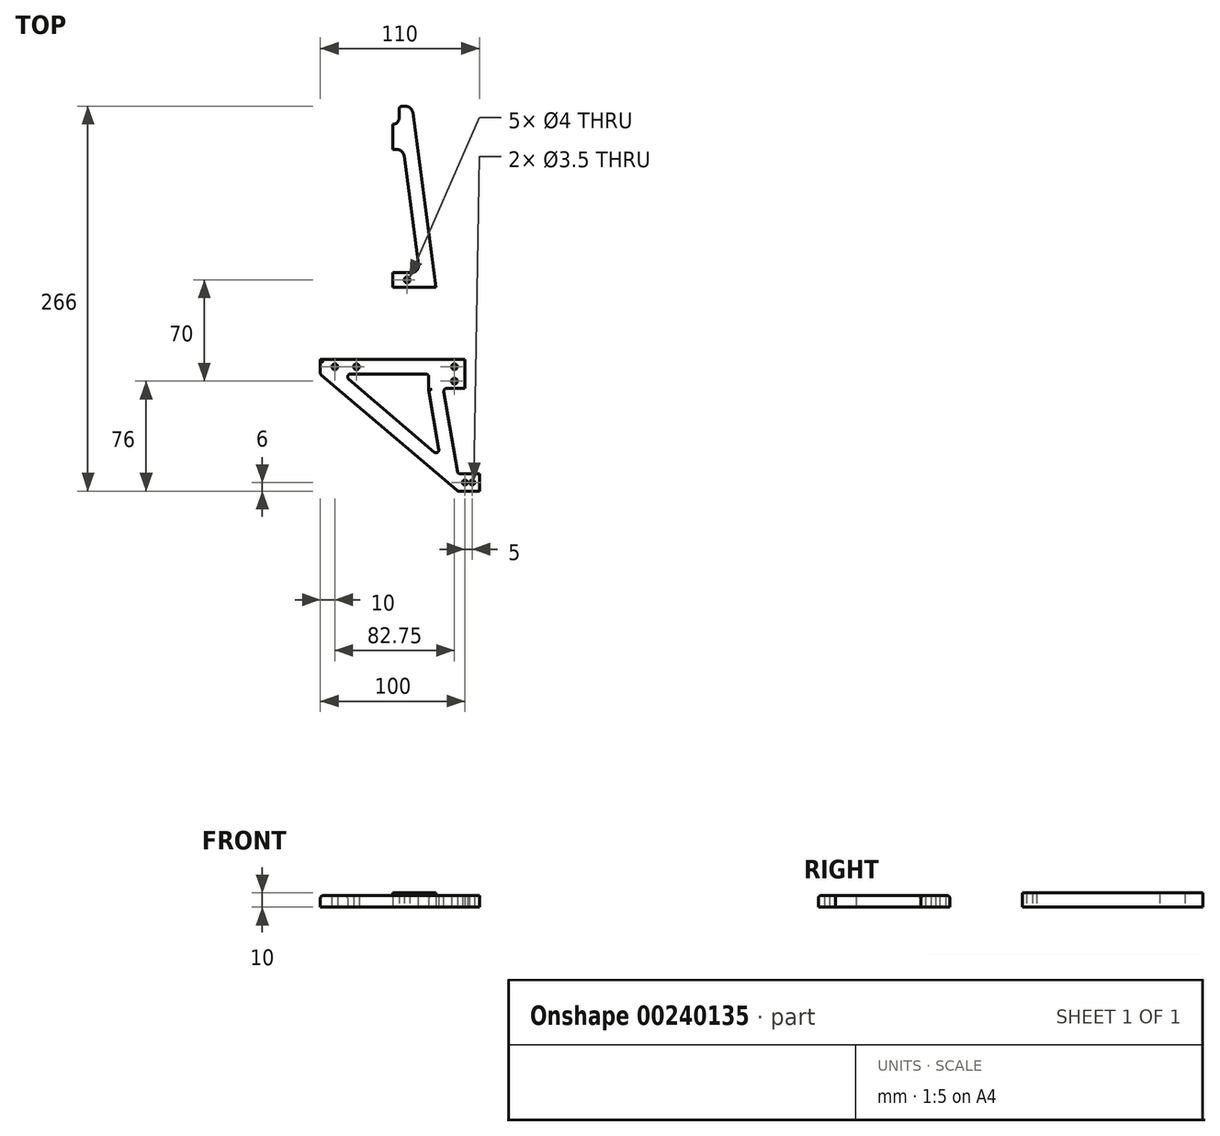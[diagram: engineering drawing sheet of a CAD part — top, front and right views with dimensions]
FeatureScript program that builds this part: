
annotation { "Feature Type Name" : "Feature", "Feature Type Description" : "" }
export const myFeature = defineFeature(function(context is Context, id is Id, definition is map)
    precondition{}
    {
        {
            var Q0;
            Q0=qCreatedBy(makeId("Top.planeOp"),FACE);
            var sketch = newSketch(context, id + "F0", { "sketchPlane" : qUnion([Q0])});
            skLineSegment(sketch, "E0.top", {"start": v(0, 75) * mm, "end": v(-30, 75) * mm});
            skPoint(sketch, "E0.middle", {"position": v(0, 0) * mm});
            skLineSegment(sketch, "E1", {"start": v(-30, 75) * mm, "end": v(-50, -75) * mm});
            skPoint(sketch, "E0.right.end.orphan", {"position": v(-50, 75) * mm});
            skPoint(sketch, "E0.left.end.orphan", {"position": v(50, 75) * mm});
            skLineSegment(sketch, "E2", {"start": v(0, 0) * mm, "end": v(0, 6) * mm});
            skLineSegment(sketch, "E3", {"start": v(-50, -75) * mm, "end": v(-40, -75) * mm});
            skLineSegment(sketch, "E4", {"start": v(-30, 75) * mm, "end": v(-20, 75) * mm});
            skLineSegment(sketch, "E5", {"start": v(0, 75) * mm, "end": v(0, 65) * mm});
            skLineSegment(sketch, "E6", {"start": v(0, 65) * mm, "end": v(-21.33, 65) * mm});
            skLineSegment(sketch, "E7", {"start": v(0, -75) * mm, "end": v(0, -65) * mm});
            skLineSegment(sketch, "E8", {"start": v(0, -65) * mm, "end": v(-38.67, -65) * mm});
            skLineSegment(sketch, "E9", {"start": v(0, 6) * mm, "end": v(-29.2, 6) * mm});
            skLineSegment(sketch, "E10", {"start": v(0, 0) * mm, "end": v(0, -6) * mm});
            skLineSegment(sketch, "E11", {"start": v(0, -6) * mm, "end": v(-30.8, -6) * mm});
            skLineSegment(sketch, "E12.trimOffspring", {"start": v(-30.8, -6) * mm, "end": v(-38.67, -65) * mm});
            skLineSegment(sketch, "E13", {"start": v(-21.33, 65) * mm, "end": v(-29.2, 6) * mm});
            skLineSegment(sketch, "E14.trimOffspring", {"start": v(0, -75) * mm, "end": v(-50, -75) * mm});
            skPoint(sketch, "E0.bottom.start.orphan", {"position": v(50, -75) * mm});
            skCircle(sketch, "E15", {"center": v(-15, 0) * mm, "radius": 2 * mm});
            skLineSegment(sketch, "E16", {"start": v(0, 65) * mm, "end": v(0, 70) * mm});
            skCircle(sketch, "E17", {"center": v(-10.41, 70) * mm, "radius": 2 * mm});
            skSolve(sketch);
        }
        {
            var Q0;
            Q0=qSketchRegion(id+"F0",true);
            extrude(context, id + "F1", {"entities" : qUnion([Q0]), "depth" : 10 * mm});
        }
        {
            var Q0;
            Q0=makeQuery(id+"F1.opExtrude","SWEPT_EDGE",EDGE,{"disambiguationData":[OSD([sQuery(id+"F0.wireOp",EDGE,"E6"),sQuery(id+"F0.wireOp",EDGE,"E13")])]});
            var Q1;
            Q1=makeQuery(id+"F1.opExtrude","SWEPT_EDGE",EDGE,{"disambiguationData":[OSD([sQuery(id+"F0.wireOp",EDGE,"E11"),sQuery(id+"F0.wireOp",EDGE,"E12.trimOffspring")])]});
            var Q2;
            Q2=makeQuery(id+"F1.opExtrude","SWEPT_EDGE",EDGE,{"disambiguationData":[OSD([sQuery(id+"F0.wireOp",EDGE,"E9"),sQuery(id+"F0.wireOp",EDGE,"E13")])]});
            var Q3;
            Q3=makeQuery(id+"F1.opExtrude","SWEPT_EDGE",EDGE,{"disambiguationData":[OSD([sQuery(id+"F0.wireOp",EDGE,"E8"),sQuery(id+"F0.wireOp",EDGE,"E12.trimOffspring")])]});
            var Q4;
            Q4=makeQuery(id+"F1.opExtrude","SWEPT_EDGE",EDGE,{"disambiguationData":[OSD([sQuery(id+"F0.wireOp",EDGE,"E1"),sQuery(id+"F0.wireOp",EDGE,"E14.trimOffspring")])]});
            fillet(context, id + "F2", {"entities" : qUnion([Q0, Q1, Q2, Q3, Q4]), "radius" : 5 * mm, "tangentPropagation" : true, "allowEdgeOverflow" : false});
        }
        {
            var Q0;
            Q0=makeQuery(id+"F1.opExtrude","SWEPT_BODY",BODY,{"disambiguationData":[OSD([sQuery(id+"F0.wireOp",EDGE,"E0.top"),sQuery(id+"F0.wireOp",EDGE,"E1"),sQuery(id+"F0.wireOp",EDGE,"E2"),sQuery(id+"F0.wireOp",EDGE,"E4"),sQuery(id+"F0.wireOp",EDGE,"E5"),sQuery(id+"F0.wireOp",EDGE,"E6"),sQuery(id+"F0.wireOp",EDGE,"E7"),sQuery(id+"F0.wireOp",EDGE,"E8"),sQuery(id+"F0.wireOp",EDGE,"E9"),sQuery(id+"F0.wireOp",EDGE,"E10"),sQuery(id+"F0.wireOp",EDGE,"E11"),sQuery(id+"F0.wireOp",EDGE,"E12.trimOffspring"),sQuery(id+"F0.wireOp",EDGE,"E13"),sQuery(id+"F0.wireOp",EDGE,"E14.trimOffspring"),sQuery(id+"F0.wireOp",EDGE,"E15"),sQuery(id+"F0.wireOp",EDGE,"E16"),sQuery(id+"F0.wireOp",EDGE,"E17")])]});
            var Q1;
            Q1=qCreatedBy(makeId("Right.planeOp"),FACE);
            mirror(context, id + "F3", {"operationType" : NewBodyOperationType.ADD, "entities" : qUnion([Q0]), "mirrorPlane" : qUnion([Q1])});
        }
        {
            var Q0;
            Q0=qCreatedBy(makeId("Top.planeOp"),FACE);
            var sketch = newSketch(context, id + "F4", { "sketchPlane" : qUnion([Q0])});
            skLineSegment(sketch, "E18", {"start": v(0, 0) * mm, "end": v(40, 0) * mm});
            skLineSegment(sketch, "E19", {"start": v(0, 75) * mm, "end": v(30, 75) * mm});
            skLineSegment(sketch, "E20", {"start": v(0, 75) * mm, "end": v(0, 85) * mm});
            skLineSegment(sketch, "E21", {"start": v(4.5, 200) * mm, "end": v(13.33, 200) * mm});
            skLineSegment(sketch, "E22", {"start": v(30, 75) * mm, "end": v(13.33, 200) * mm});
            skArc(sketch, "E23", {"start": v(0, 187.5) * mm, "mid": v(3.18, 188.82) * mm, "end": v(4.5, 192) * mm});
            skLineSegment(sketch, "E24", {"start": v(4.5, 200) * mm, "end": v(4.5, 192) * mm});
            skLineSegment(sketch, "E25", {"start": v(0, 75) * mm, "end": v(0, 80) * mm});
            skCircle(sketch, "E26", {"center": v(10, 80) * mm, "radius": 2 * mm});
            skLineSegment(sketch, "E27", {"start": v(0, 75) * mm, "end": v(10, 75) * mm});
            skLineSegment(sketch, "E28", {"start": v(10, 85) * mm, "end": v(18.67, 85) * mm});
            skLineSegment(sketch, "E29", {"start": v(18.67, 85) * mm, "end": v(10, 150) * mm});
            skLineSegment(sketch, "E30", {"start": v(10, 85) * mm, "end": v(0, 85) * mm});
            skLineSegment(sketch, "E31", {"start": v(18.67, 85) * mm, "end": v(7.31, 170.17) * mm});
            skLineSegment(sketch, "E32", {"start": v(7.31, 170.17) * mm, "end": v(0, 170.17) * mm});
            skLineSegment(sketch, "E33.trimOffspring", {"start": v(0, 170.17) * mm, "end": v(0, 187.5) * mm});
            skSolve(sketch);
        }
        {
            var Q0;
            Q0=qSketchRegion(id+"F4",true);
            extrude(context, id + "F5", {"entities" : qUnion([Q0]), "depth" : 10 * mm});
        }
        {
            var Q0;
            Q0=makeQuery(id+"F5.opExtrude","SWEPT_BODY",BODY,{"disambiguationData":[OSD([sQuery(id+"F4.wireOp",EDGE,"E19"),sQuery(id+"F4.wireOp",EDGE,"E20"),sQuery(id+"F4.wireOp",EDGE,"E21"),sQuery(id+"F4.wireOp",EDGE,"E22"),sQuery(id+"F4.wireOp",EDGE,"E23"),sQuery(id+"F4.wireOp",EDGE,"E24"),sQuery(id+"F4.wireOp",EDGE,"E25"),sQuery(id+"F4.wireOp",EDGE,"E26"),sQuery(id+"F4.wireOp",EDGE,"E27"),sQuery(id+"F4.wireOp",EDGE,"E28"),sQuery(id+"F4.wireOp",EDGE,"E30"),sQuery(id+"F4.wireOp",EDGE,"E31"),sQuery(id+"F4.wireOp",EDGE,"E32"),sQuery(id+"F4.wireOp",EDGE,"E33.trimOffspring")])]});
            var Q1;
            Q1=qCreatedBy(makeId("Right.planeOp"),FACE);
            mirror(context, id + "F6", {"entities" : qUnion([Q0]), "mirrorPlane" : qUnion([Q1])});
        }
        {
            var Q0;
            Q0=makeQuery(id+"F6.opPattern","COPY",EDGE,{"derivedFrom":makeQuery(id+"F5.opExtrude","SWEPT_EDGE",EDGE,{"disambiguationData":[OSD([sQuery(id+"F4.wireOp",EDGE,"E31"),sQuery(id+"F4.wireOp",EDGE,"E32")])]}),"instanceName":"1"});
            var Q1;
            Q1=makeQuery(id+"F5.opExtrude","SWEPT_EDGE",EDGE,{"disambiguationData":[OSD([sQuery(id+"F4.wireOp",EDGE,"E31"),sQuery(id+"F4.wireOp",EDGE,"E32")])]});
            var Q2;
            Q2=makeQuery(id+"F6.opPattern","COPY",EDGE,{"derivedFrom":makeQuery(id+"F5.opExtrude","SWEPT_EDGE",EDGE,{"disambiguationData":[OSD([sQuery(id+"F4.wireOp",EDGE,"E28"),sQuery(id+"F4.wireOp",EDGE,"E31")])]}),"instanceName":"1"});
            var Q3;
            Q3=makeQuery(id+"F5.opExtrude","SWEPT_EDGE",EDGE,{"disambiguationData":[OSD([sQuery(id+"F4.wireOp",EDGE,"E28"),sQuery(id+"F4.wireOp",EDGE,"E31")])]});
            var Q4;
            Q4=makeQuery(id+"F6.opPattern","COPY",EDGE,{"derivedFrom":makeQuery(id+"F5.opExtrude","SWEPT_EDGE",EDGE,{"disambiguationData":[OSD([sQuery(id+"F4.wireOp",EDGE,"E21"),sQuery(id+"F4.wireOp",EDGE,"E22")])]}),"instanceName":"1"});
            var Q5;
            Q5=makeQuery(id+"F5.opExtrude","SWEPT_EDGE",EDGE,{"disambiguationData":[OSD([sQuery(id+"F4.wireOp",EDGE,"E21"),sQuery(id+"F4.wireOp",EDGE,"E22")])]});
            fillet(context, id + "F7", {"entities" : qUnion([Q0, Q1, Q2, Q3, Q4, Q5]), "radius" : 5 * mm, "tangentPropagation" : true, "allowEdgeOverflow" : false});
        }
        {
            var Q0;
            Q0=makeQuery(id+"F5.opExtrude","SWEPT_EDGE",EDGE,{"disambiguationData":[OSD([sQuery(id+"F4.wireOp",EDGE,"E21"),sQuery(id+"F4.wireOp",EDGE,"E24")])]});
            var Q1;
            Q1=makeQuery(id+"F6.opPattern","COPY",EDGE,{"derivedFrom":makeQuery(id+"F5.opExtrude","SWEPT_EDGE",EDGE,{"disambiguationData":[OSD([sQuery(id+"F4.wireOp",EDGE,"E21"),sQuery(id+"F4.wireOp",EDGE,"E24")])]}),"instanceName":"1"});
            fillet(context, id + "F8", {"entities" : qUnion([Q0, Q1]), "radius" : 2 * mm, "tangentPropagation" : true, "allowEdgeOverflow" : false});
        }
        {
            var Q0;
            Q0=qCreatedBy(makeId("Top.planeOp"),FACE);
            var sketch = newSketch(context, id + "F9", { "sketchPlane" : qUnion([Q0])});
            skLineSegment(sketch, "E34", {"start": v(0, 0) * mm, "end": v(0, 6) * mm});
            skLineSegment(sketch, "E35", {"start": v(0, 6) * mm, "end": v(-6, 6) * mm});
            skLineSegment(sketch, "E36", {"start": v(-6, 6) * mm, "end": v(-6, -6) * mm});
            skLineSegment(sketch, "E37", {"start": v(-6, -6) * mm, "end": v(0, -6) * mm});
            skLineSegment(sketch, "E38", {"start": v(0, -6) * mm, "end": v(0, 0) * mm});
            skSolve(sketch);
        }
        {
            var Q0;
            Q0=qSketchRegion(id+"F9",true);
            extrude(context, id + "F10", {"entities" : qUnion([Q0]), "operationType" : NewBodyOperationType.ADD, "depth" : 25 * mm});
        }
        {
            var Q0;
            Q0=makeQuery(id+"F10.opExtrude","SWEPT_EDGE",EDGE,{"disambiguationData":[OSD([sQuery(id+"F9.wireOp",EDGE,"E36"),sQuery(id+"F9.wireOp",EDGE,"E37")])]});
            var Q1;
            Q1=makeQuery(id+"F10.opExtrude","CAP_EDGE",EDGE,{"disambiguationData":[OSD([sQuery(id+"F9.wireOp",EDGE,"E36")])],"isStart":false});
            var Q2;
            Q2=makeQuery(id+"F10.opExtrude","CAP_EDGE",EDGE,{"disambiguationData":[OSD([sQuery(id+"F9.wireOp",EDGE,"E37")])],"isStart":false});
            var Q3;
            Q3=makeQuery(id+"F10.opExtrude","SWEPT_EDGE",EDGE,{"disambiguationData":[OSD([sQuery(id+"F9.wireOp",EDGE,"E35"),sQuery(id+"F9.wireOp",EDGE,"E36")])]});
            var Q4;
            Q4=makeQuery(id+"F10.opExtrude","CAP_EDGE",EDGE,{"disambiguationData":[OSD([sQuery(id+"F9.wireOp",EDGE,"E35")])],"isStart":false});
            fillet(context, id + "F11", {"entities" : qUnion([Q0, Q1, Q2, Q3, Q4]), "radius" : 1.5 * mm, "tangentPropagation" : true, "allowEdgeOverflow" : false});
        }
        {
            var Q0;
            Q0=qCreatedBy(makeId("Right.planeOp"),FACE);
            var sketch = newSketch(context, id + "F12", { "sketchPlane" : qUnion([Q0])});
            skCircle(sketch, "E39", {"center": v(0, 20) * mm, "radius": 1.75 * mm});
            skCircle(sketch, "E40", {"center": v(0, 15) * mm, "radius": 1.75 * mm});
            skSolve(sketch);
        }
        {
            var Q0;
            Q0=qSketchRegion(id+"F12",true);
            extrude(context, id + "F13", {"entities" : qUnion([Q0]), "endBound" : BoundingType.SYMMETRIC, "depth" : 25 * mm});
        }
        {
            var Q0;
            Q0=makeQuery(id+"F13.opExtrude","SWEPT_BODY",BODY,{"disambiguationData":[OSD([sQuery(id+"F12.wireOp",EDGE,"E40")])]});
            var Q1;
            Q1=makeQuery(id+"F13.opExtrude","SWEPT_BODY",BODY,{"disambiguationData":[OSD([sQuery(id+"F12.wireOp",EDGE,"E39")])]});
            var Q2;
            Q2=makeQuery(id+"F1.opExtrude","SWEPT_BODY",BODY,{"disambiguationData":[OSD([sQuery(id+"F0.wireOp",EDGE,"E0.top"),sQuery(id+"F0.wireOp",EDGE,"E1"),sQuery(id+"F0.wireOp",EDGE,"E2"),sQuery(id+"F0.wireOp",EDGE,"E4"),sQuery(id+"F0.wireOp",EDGE,"E5"),sQuery(id+"F0.wireOp",EDGE,"E6"),sQuery(id+"F0.wireOp",EDGE,"E7"),sQuery(id+"F0.wireOp",EDGE,"E8"),sQuery(id+"F0.wireOp",EDGE,"E9"),sQuery(id+"F0.wireOp",EDGE,"E10"),sQuery(id+"F0.wireOp",EDGE,"E11"),sQuery(id+"F0.wireOp",EDGE,"E12.trimOffspring"),sQuery(id+"F0.wireOp",EDGE,"E13"),sQuery(id+"F0.wireOp",EDGE,"E14.trimOffspring"),sQuery(id+"F0.wireOp",EDGE,"E15"),sQuery(id+"F0.wireOp",EDGE,"E16"),sQuery(id+"F0.wireOp",EDGE,"E17")])]});
            booleanBodies(context, id + "F14", {"operationType" : BooleanOperationType.SUBTRACTION, "tools" : qUnion([Q0, Q1]), "targets" : qUnion([Q2])});
        }
        {
            var Q0;
            Q0=qCreatedBy(makeId("Top.planeOp"),FACE);
            var sketch = newSketch(context, id + "F15", { "sketchPlane" : qUnion([Q0])});
            skLineSegment(sketch, "E41.bottom", {"start": v(15, 65) * mm, "end": v(-15, 65) * mm});
            skLineSegment(sketch, "E41.top", {"start": v(15, 85) * mm, "end": v(-15, 85) * mm});
            skLineSegment(sketch, "E41.left", {"start": v(15, 65) * mm, "end": v(15, 85) * mm});
            skLineSegment(sketch, "E41.right", {"start": v(-15, 65) * mm, "end": v(-15, 85) * mm});
            skPoint(sketch, "E41.middle", {"position": v(0, 75) * mm});
            skLineSegment(sketch, "E42", {"start": v(0, 75) * mm, "end": v(0, 85) * mm});
            skLineSegment(sketch, "E43", {"start": v(0, 85) * mm, "end": v(0, 65) * mm});
            skLineSegment(sketch, "E44", {"start": v(0, 65) * mm, "end": v(-6, 65) * mm});
            skLineSegment(sketch, "E45", {"start": v(-6, 65) * mm, "end": v(-6, 85) * mm});
            skLineSegment(sketch, "E46", {"start": v(-6, 85) * mm, "end": v(0, 85) * mm});
            skSolve(sketch);
        }
        {
            var Q0;
            Q0=qSketchRegion(id+"F15",true);
            extrude(context, id + "F16", {"entities" : qUnion([Q0]), "depth" : 10 * mm});
        }
        {
            var Q0;
            Q0=qCreatedBy(makeId("Top.planeOp"),FACE);
            var sketch = newSketch(context, id + "F17", { "sketchPlane" : qUnion([Q0])});
            skLineSegment(sketch, "E47", {"start": v(0, 65) * mm, "end": v(0, 85) * mm});
            skLineSegment(sketch, "E48", {"start": v(0, 85) * mm, "end": v(-6, 85) * mm});
            skLineSegment(sketch, "E49", {"start": v(-6, 85) * mm, "end": v(-6, 65) * mm});
            skLineSegment(sketch, "E50", {"start": v(-6, 65) * mm, "end": v(0, 65) * mm});
            skSolve(sketch);
        }
        {
            var Q0;
            Q0=qSketchRegion(id+"F17",true);
            extrude(context, id + "F18", {"entities" : qUnion([Q0]), "depth" : 25 * mm});
        }
        {
            var Q0;
            Q0=makeQuery(id+"F16.opExtrude","SWEPT_BODY",BODY,{"disambiguationData":[OSD([sQuery(id+"F15.wireOp",EDGE,"E41.bottom"),sQuery(id+"F15.wireOp",EDGE,"E41.top"),sQuery(id+"F15.wireOp",EDGE,"E41.left"),sQuery(id+"F15.wireOp",EDGE,"E41.right"),sQuery(id+"F15.wireOp",EDGE,"E44"),sQuery(id+"F15.wireOp",EDGE,"E46")])]});
            var Q1;
            Q1=makeQuery(id+"F18.opExtrude","SWEPT_BODY",BODY,{"disambiguationData":[OSD([sQuery(id+"F17.wireOp",EDGE,"E47"),sQuery(id+"F17.wireOp",EDGE,"E48"),sQuery(id+"F17.wireOp",EDGE,"E49"),sQuery(id+"F17.wireOp",EDGE,"E50")])]});
            booleanBodies(context, id + "F19", {"operationType" : BooleanOperationType.UNION, "tools" : qUnion([Q0, Q1])});
        }
        {
            var Q0;
            Q0=makeQuery(id+"F16.opExtrude","SWEPT_BODY",BODY,{"disambiguationData":[OSD([sQuery(id+"F15.wireOp",EDGE,"E41.bottom"),sQuery(id+"F15.wireOp",EDGE,"E41.top"),sQuery(id+"F15.wireOp",EDGE,"E41.left"),sQuery(id+"F15.wireOp",EDGE,"E41.right"),sQuery(id+"F15.wireOp",EDGE,"E44"),sQuery(id+"F15.wireOp",EDGE,"E46")])]});
            transform(context, id + "F20", {"entities" : qUnion([Q0]), "transformType" : TransformType.TRANSLATION_3D, "dx" : 0 * mm, "dy" : 0 * mm, "dz" : 10 * mm, "makeCopy" : false});
        }
        {
            var Q0;
            Q0=qCreatedBy(makeId("Top.planeOp"),FACE);
            var sketch = newSketch(context, id + "F21", { "sketchPlane" : qUnion([Q0])});
            skCircle(sketch, "E51", {"center": v(-10, 80) * mm, "radius": 2 * mm});
            skCircle(sketch, "E52", {"center": v(10, 80) * mm, "radius": 2 * mm});
            skCircle(sketch, "E53", {"center": v(-10.4, 70) * mm, "radius": 2 * mm});
            skCircle(sketch, "E54", {"center": v(10.4, 70) * mm, "radius": 2 * mm});
            skSolve(sketch);
        }
        {
            var Q0;
            Q0=qSketchRegion(id+"F21",true);
            extrude(context, id + "F22", {"entities" : qUnion([Q0]), "depth" : 30 * mm});
        }
        {
            var Q0;
            Q0=makeQuery(id+"F22.opExtrude","SWEPT_BODY",BODY,{"disambiguationData":[OSD([sQuery(id+"F21.wireOp",EDGE,"E54")])]});
            var Q1;
            Q1=makeQuery(id+"F22.opExtrude","SWEPT_BODY",BODY,{"disambiguationData":[OSD([sQuery(id+"F21.wireOp",EDGE,"E53")])]});
            var Q2;
            Q2=makeQuery(id+"F22.opExtrude","SWEPT_BODY",BODY,{"disambiguationData":[OSD([sQuery(id+"F21.wireOp",EDGE,"E52")])]});
            var Q3;
            Q3=makeQuery(id+"F22.opExtrude","SWEPT_BODY",BODY,{"disambiguationData":[OSD([sQuery(id+"F21.wireOp",EDGE,"E51")])]});
            var Q4;
            Q4=makeQuery(id+"F16.opExtrude","SWEPT_BODY",BODY,{"disambiguationData":[OSD([sQuery(id+"F15.wireOp",EDGE,"E41.bottom"),sQuery(id+"F15.wireOp",EDGE,"E41.top"),sQuery(id+"F15.wireOp",EDGE,"E41.left"),sQuery(id+"F15.wireOp",EDGE,"E41.right"),sQuery(id+"F15.wireOp",EDGE,"E44"),sQuery(id+"F15.wireOp",EDGE,"E46")])]});
            booleanBodies(context, id + "F23", {"operationType" : BooleanOperationType.SUBTRACTION, "tools" : qUnion([Q0, Q1, Q2, Q3]), "targets" : qUnion([Q4])});
        }
        {
            var Q0;
            Q0=qCreatedBy(makeId("Right.planeOp"),FACE);
            var sketch = newSketch(context, id + "F24", { "sketchPlane" : qUnion([Q0])});
            skCircle(sketch, "E55", {"center": v(80, 27.23) * mm, "radius": 2 * mm});
            skCircle(sketch, "E56", {"center": v(70, 27.23) * mm, "radius": 2 * mm});
            skSolve(sketch);
        }
        {
            var Q0;
            Q0=qSketchRegion(id+"F24",true);
            extrude(context, id + "F25", {"entities" : qUnion([Q0]), "endBound" : BoundingType.SYMMETRIC, "depth" : 25 * mm});
        }
        {
            var Q0;
            Q0=makeQuery(id+"F25.opExtrude","SWEPT_BODY",BODY,{"disambiguationData":[OSD([sQuery(id+"F24.wireOp",EDGE,"E56")])]});
            var Q1;
            Q1=makeQuery(id+"F25.opExtrude","SWEPT_BODY",BODY,{"disambiguationData":[OSD([sQuery(id+"F24.wireOp",EDGE,"E55")])]});
            var Q2;
            Q2=makeQuery(id+"F16.opExtrude","SWEPT_BODY",BODY,{"disambiguationData":[OSD([sQuery(id+"F15.wireOp",EDGE,"E41.bottom"),sQuery(id+"F15.wireOp",EDGE,"E41.top"),sQuery(id+"F15.wireOp",EDGE,"E41.left"),sQuery(id+"F15.wireOp",EDGE,"E41.right"),sQuery(id+"F15.wireOp",EDGE,"E44"),sQuery(id+"F15.wireOp",EDGE,"E46")])]});
            booleanBodies(context, id + "F26", {"operationType" : BooleanOperationType.SUBTRACTION, "tools" : qUnion([Q0, Q1]), "targets" : qUnion([Q2])});
        }
        {
            var Q0;
            Q0=makeQuery(id+"F18.opExtrude","SWEPT_EDGE",EDGE,{"disambiguationData":[OSD([sQuery(id+"F17.wireOp",EDGE,"E49"),sQuery(id+"F17.wireOp",EDGE,"E50")])]});
            var Q1;
            Q1=makeQuery(id+"F18.opExtrude","CAP_EDGE",EDGE,{"disambiguationData":[OSD([sQuery(id+"F17.wireOp",EDGE,"E50")])],"isStart":false});
            var Q2;
            {var subQ0=sQuery(id+"F15.wireOp",EDGE,"E44");var subQ1=sQuery(id+"F15.wireOp",EDGE,"E41.bottom");var subQ2=sQuery(id+"F15.wireOp",EDGE,"E41.right");Q2=makeQuery(id+"F19.opBoolean","SPLIT",EDGE,{"disambiguationData":[TD([makeQuery(id+"F16.opExtrude","SWEPT_FACE",FACE,{"disambiguationData":[OSD([subQ2])]})])],"derivedFrom":makeQuery(id+"F16.opExtrude","CAP_EDGE",EDGE,{"disambiguationData":[OSD([subQ1,subQ0])],"isStart":false})});}
            var Q3;
            Q3=makeQuery(id+"F16.opExtrude","SWEPT_EDGE",EDGE,{"disambiguationData":[OSD([sQuery(id+"F15.wireOp",EDGE,"E41.bottom"),sQuery(id+"F15.wireOp",EDGE,"E41.right")])]});
            var Q4;
            {var subQ0=sQuery(id+"F15.wireOp",EDGE,"E41.left");var subQ1=sQuery(id+"F15.wireOp",EDGE,"E44");var subQ2=sQuery(id+"F15.wireOp",EDGE,"E41.bottom");Q4=makeQuery(id+"F19.opBoolean","SPLIT",EDGE,{"disambiguationData":[TD([makeQuery(id+"F16.opExtrude","SWEPT_FACE",FACE,{"disambiguationData":[OSD([subQ0])]})])],"derivedFrom":makeQuery(id+"F16.opExtrude","CAP_EDGE",EDGE,{"disambiguationData":[OSD([subQ2,subQ1])],"isStart":false})});}
            var Q5;
            Q5=makeQuery(id+"F16.opExtrude","SWEPT_EDGE",EDGE,{"disambiguationData":[OSD([sQuery(id+"F15.wireOp",EDGE,"E41.bottom"),sQuery(id+"F15.wireOp",EDGE,"E41.left")])]});
            var Q6;
            Q6=makeQuery(id+"F16.opExtrude","CAP_EDGE",EDGE,{"disambiguationData":[OSD([sQuery(id+"F15.wireOp",EDGE,"E41.left")])],"isStart":false});
            var Q7;
            Q7=makeQuery(id+"F16.opExtrude","CAP_EDGE",EDGE,{"disambiguationData":[OSD([sQuery(id+"F15.wireOp",EDGE,"E41.right")])],"isStart":false});
            var Q8;
            Q8=makeQuery(id+"F18.opExtrude","CAP_EDGE",EDGE,{"disambiguationData":[OSD([sQuery(id+"F17.wireOp",EDGE,"E49")])],"isStart":false});
            var Q9;
            {var subQ0=sQuery(id+"F15.wireOp",EDGE,"E41.right");var subQ1=sQuery(id+"F15.wireOp",EDGE,"E46");var subQ2=sQuery(id+"F15.wireOp",EDGE,"E41.top");Q9=makeQuery(id+"F19.opBoolean","SPLIT",EDGE,{"disambiguationData":[TD([makeQuery(id+"F16.opExtrude","SWEPT_FACE",FACE,{"disambiguationData":[OSD([subQ0])]})])],"derivedFrom":makeQuery(id+"F16.opExtrude","CAP_EDGE",EDGE,{"disambiguationData":[OSD([subQ2,subQ1])],"isStart":false})});}
            var Q10;
            Q10=makeQuery(id+"F16.opExtrude","SWEPT_EDGE",EDGE,{"disambiguationData":[OSD([sQuery(id+"F15.wireOp",EDGE,"E41.top"),sQuery(id+"F15.wireOp",EDGE,"E41.right")])]});
            var Q11;
            Q11=makeQuery(id+"F18.opExtrude","SWEPT_EDGE",EDGE,{"disambiguationData":[OSD([sQuery(id+"F17.wireOp",EDGE,"E48"),sQuery(id+"F17.wireOp",EDGE,"E49")])]});
            var Q12;
            Q12=makeQuery(id+"F18.opExtrude","CAP_EDGE",EDGE,{"disambiguationData":[OSD([sQuery(id+"F17.wireOp",EDGE,"E48")])],"isStart":false});
            var Q13;
            {var subQ0=sQuery(id+"F15.wireOp",EDGE,"E41.left");var subQ1=sQuery(id+"F15.wireOp",EDGE,"E46");var subQ2=sQuery(id+"F15.wireOp",EDGE,"E41.top");Q13=makeQuery(id+"F19.opBoolean","SPLIT",EDGE,{"disambiguationData":[TD([makeQuery(id+"F16.opExtrude","SWEPT_FACE",FACE,{"disambiguationData":[OSD([subQ0])]})])],"derivedFrom":makeQuery(id+"F16.opExtrude","CAP_EDGE",EDGE,{"disambiguationData":[OSD([subQ2,subQ1])],"isStart":false})});}
            var Q14;
            Q14=makeQuery(id+"F16.opExtrude","SWEPT_EDGE",EDGE,{"disambiguationData":[OSD([sQuery(id+"F15.wireOp",EDGE,"E41.top"),sQuery(id+"F15.wireOp",EDGE,"E41.left")])]});
            fillet(context, id + "F27", {"entities" : qUnion([Q0, Q1, Q2, Q3, Q4, Q5, Q6, Q7, Q8, Q9, Q10, Q11, Q12, Q13, Q14]), "radius" : 2 * mm, "tangentPropagation" : true, "allowEdgeOverflow" : false});
        }
        {
            var Q0;
            Q0=qCreatedBy(makeId("Right.planeOp"),FACE);
            var sketch = newSketch(context, id + "F28", { "sketchPlane" : qUnion([Q0])});
            skLineSegment(sketch, "E57", {"start": v(0, 0) * mm, "end": v(0, 10) * mm});
            skLineSegment(sketch, "E58", {"start": v(0, 10) * mm, "end": v(6, 10) * mm});
            skLineSegment(sketch, "E59", {"start": v(6, 10) * mm, "end": v(6, 25) * mm});
            skLineSegment(sketch, "E60", {"start": v(-6, 25) * mm, "end": v(-6, 10) * mm});
            skLineSegment(sketch, "E61", {"start": v(-6, 10) * mm, "end": v(0, 10) * mm});
            skLineSegment(sketch, "E62", {"start": v(75, 10) * mm, "end": v(75, 20) * mm});
            skLineSegment(sketch, "E63", {"start": v(75, 20) * mm, "end": v(85, 20) * mm});
            skLineSegment(sketch, "E64", {"start": v(85, 20) * mm, "end": v(85, 35) * mm});
            skLineSegment(sketch, "E65", {"start": v(65, 35) * mm, "end": v(65, 20) * mm});
            skLineSegment(sketch, "E66", {"start": v(65, 20) * mm, "end": v(75, 20) * mm});
            skLineSegment(sketch, "E67", {"start": v(-6, 10) * mm, "end": v(-6, 25) * mm});
            skLineSegment(sketch, "E68", {"start": v(75, 120) * mm, "end": v(85, 120) * mm});
            skLineSegment(sketch, "E69", {"start": v(85, 35) * mm, "end": v(85, 120) * mm});
            skLineSegment(sketch, "E70", {"start": v(85, 120) * mm, "end": v(75, 120) * mm});
            skLineSegment(sketch, "E71", {"start": v(6, 25) * mm, "end": v(65, 35) * mm});
            skLineSegment(sketch, "E72", {"start": v(-6, 25) * mm, "end": v(75, 120) * mm});
            skLineSegment(sketch, "E73", {"start": v(23.92, 44.68) * mm, "end": v(75, 104.59) * mm});
            skLineSegment(sketch, "E74", {"start": v(23.92, 44.68) * mm, "end": v(17.44, 37.08) * mm});
            skLineSegment(sketch, "E75", {"start": v(75, 45) * mm, "end": v(64.16, 45) * mm});
            skLineSegment(sketch, "E76", {"start": v(51.92, 42.93) * mm, "end": v(17.44, 37.08) * mm});
            skLineSegment(sketch, "E77", {"start": v(51.92, 42.93) * mm, "end": v(64.16, 45) * mm});
            skPoint(sketch, "E78.orphan", {"position": v(75, 35) * mm});
            skPoint(sketch, "E79.start.orphan", {"position": v(75, 110) * mm});
            skLineSegment(sketch, "E80", {"start": v(75, 104.59) * mm, "end": v(75, 45) * mm});
            skCircle(sketch, "E81", {"center": v(80, 110) * mm, "radius": 2 * mm});
            skCircle(sketch, "E82", {"center": v(80, 95) * mm, "radius": 2 * mm});
            skPoint(sketch, "E83.end.orphan", {"position": v(80, 120) * mm});
            skSolve(sketch);
        }
        {
            var Q0;
            Q0=qSketchRegion(id+"F28",true);
            extrude(context, id + "F29", {"entities" : qUnion([Q0]), "depth" : 8 * mm});
        }
        {
            var Q0;
            Q0=makeQuery(id+"F29.opExtrude","SWEPT_EDGE",EDGE,{"disambiguationData":[OSD([sQuery(id+"F28.wireOp",EDGE,"E73"),sQuery(id+"F28.wireOp",EDGE,"E80")])]});
            var Q1;
            Q1=makeQuery(id+"F29.opExtrude","SWEPT_EDGE",EDGE,{"disambiguationData":[OSD([sQuery(id+"F28.wireOp",EDGE,"E75"),sQuery(id+"F28.wireOp",EDGE,"E80")])]});
            var Q2;
            Q2=makeQuery(id+"F29.opExtrude","SWEPT_EDGE",EDGE,{"disambiguationData":[OSD([sQuery(id+"F28.wireOp",EDGE,"E74"),sQuery(id+"F28.wireOp",EDGE,"E76")])]});
            var Q3;
            Q3=makeQuery(id+"F29.opExtrude","SWEPT_EDGE",EDGE,{"disambiguationData":[OSD([sQuery(id+"F28.wireOp",EDGE,"E65"),sQuery(id+"F28.wireOp",EDGE,"E71")])]});
            var Q4;
            Q4=makeQuery(id+"F29.opExtrude","SWEPT_EDGE",EDGE,{"disambiguationData":[OSD([sQuery(id+"F28.wireOp",EDGE,"E59"),sQuery(id+"F28.wireOp",EDGE,"E71")])]});
            var Q5;
            Q5=makeQuery(id+"F29.opExtrude","SWEPT_EDGE",EDGE,{"disambiguationData":[OSD([sQuery(id+"F28.wireOp",EDGE,"E67"),sQuery(id+"F28.wireOp",EDGE,"E72")])]});
            fillet(context, id + "F30", {"entities" : qUnion([Q0, Q1, Q2, Q3, Q4, Q5]), "radius" : 2 * mm, "tangentPropagation" : true, "allowEdgeOverflow" : false});
        }
        {
            var Q0;
            Q0=makeQuery(id+"F29.opExtrude","CAP_EDGE",EDGE,{"disambiguationData":[OSD([sQuery(id+"F28.wireOp",EDGE,"E73"),sQuery(id+"F28.wireOp",EDGE,"E74")])],"isStart":false});
            var Q1;
            Q1=makeQuery(id+"F29.opExtrude","CAP_EDGE",EDGE,{"disambiguationData":[OSD([sQuery(id+"F28.wireOp",EDGE,"E72")])],"isStart":false});
            var Q2;
            Q2=makeQuery(id+"F29.opExtrude","CAP_EDGE",EDGE,{"disambiguationData":[OSD([sQuery(id+"F28.wireOp",EDGE,"E71")])],"isStart":false});
            var Q3;
            Q3=makeQuery(id+"F29.opExtrude","CAP_EDGE",EDGE,{"disambiguationData":[OSD([sQuery(id+"F28.wireOp",EDGE,"E64"),sQuery(id+"F28.wireOp",EDGE,"E69")])],"isStart":false});
            fillet(context, id + "F31", {"entities" : qUnion([Q0, Q1, Q2, Q3]), "radius" : 2 * mm, "tangentPropagation" : true, "allowEdgeOverflow" : false});
        }
        {
            var Q0;
            Q0=qCreatedBy(makeId("Right.planeOp"),FACE);
            var sketch = newSketch(context, id + "F32", { "sketchPlane" : qUnion([Q0])});
            skCircle(sketch, "E84", {"center": v(0, 20) * mm, "radius": 1.75 * mm});
            skCircle(sketch, "E85", {"center": v(0, 15) * mm, "radius": 1.75 * mm});
            skCircle(sketch, "E86", {"center": v(70, 27.25) * mm, "radius": 2 * mm});
            skCircle(sketch, "E87", {"center": v(80, 27.25) * mm, "radius": 2 * mm});
            skSolve(sketch);
        }
        {
            var Q0;
            Q0=qSketchRegion(id+"F32",true);
            extrude(context, id + "F33", {"entities" : qUnion([Q0]), "depth" : 25 * mm});
        }
        {
            var Q0;
            Q0=makeQuery(id+"F33.opExtrude","SWEPT_BODY",BODY,{"disambiguationData":[OSD([sQuery(id+"F32.wireOp",EDGE,"E87")])]});
            var Q1;
            Q1=makeQuery(id+"F33.opExtrude","SWEPT_BODY",BODY,{"disambiguationData":[OSD([sQuery(id+"F32.wireOp",EDGE,"E86")])]});
            var Q2;
            Q2=makeQuery(id+"F33.opExtrude","SWEPT_BODY",BODY,{"disambiguationData":[OSD([sQuery(id+"F32.wireOp",EDGE,"E85")])]});
            var Q3;
            Q3=makeQuery(id+"F33.opExtrude","SWEPT_BODY",BODY,{"disambiguationData":[OSD([sQuery(id+"F32.wireOp",EDGE,"E84")])]});
            var Q4;
            Q4=makeQuery(id+"F29.opExtrude","SWEPT_BODY",BODY,{"disambiguationData":[OSD([sQuery(id+"F28.wireOp",EDGE,"E59"),sQuery(id+"F28.wireOp",EDGE,"E61"),sQuery(id+"F28.wireOp",EDGE,"E58"),sQuery(id+"F28.wireOp",EDGE,"E63"),sQuery(id+"F28.wireOp",EDGE,"E64"),sQuery(id+"F28.wireOp",EDGE,"E65"),sQuery(id+"F28.wireOp",EDGE,"E66"),sQuery(id+"F28.wireOp",EDGE,"E67"),sQuery(id+"F28.wireOp",EDGE,"E69"),sQuery(id+"F28.wireOp",EDGE,"E70"),sQuery(id+"F28.wireOp",EDGE,"E71"),sQuery(id+"F28.wireOp",EDGE,"E72"),sQuery(id+"F28.wireOp",EDGE,"E73"),sQuery(id+"F28.wireOp",EDGE,"E74"),sQuery(id+"F28.wireOp",EDGE,"E75"),sQuery(id+"F28.wireOp",EDGE,"E76"),sQuery(id+"F28.wireOp",EDGE,"E77"),sQuery(id+"F28.wireOp",EDGE,"E80"),sQuery(id+"F28.wireOp",EDGE,"E81"),sQuery(id+"F28.wireOp",EDGE,"E82")])]});
            booleanBodies(context, id + "F34", {"operationType" : BooleanOperationType.SUBTRACTION, "tools" : qUnion([Q0, Q1, Q2, Q3]), "targets" : qUnion([Q4])});
        }
        {
            var Q0;
            Q0=makeQuery(id+"F16.opExtrude","SWEPT_BODY",BODY,{"disambiguationData":[OSD([sQuery(id+"F15.wireOp",EDGE,"E41.bottom"),sQuery(id+"F15.wireOp",EDGE,"E41.top"),sQuery(id+"F15.wireOp",EDGE,"E41.left"),sQuery(id+"F15.wireOp",EDGE,"E41.right"),sQuery(id+"F15.wireOp",EDGE,"E44"),sQuery(id+"F15.wireOp",EDGE,"E46")])]});
            var Q1;
            Q1=makeQuery(id+"F6.opPattern","COPY",BODY,{"derivedFrom":makeQuery(id+"F5.opExtrude","SWEPT_BODY",BODY,{"disambiguationData":[OSD([sQuery(id+"F4.wireOp",EDGE,"E19"),sQuery(id+"F4.wireOp",EDGE,"E20"),sQuery(id+"F4.wireOp",EDGE,"E21"),sQuery(id+"F4.wireOp",EDGE,"E22"),sQuery(id+"F4.wireOp",EDGE,"E23"),sQuery(id+"F4.wireOp",EDGE,"E24"),sQuery(id+"F4.wireOp",EDGE,"E25"),sQuery(id+"F4.wireOp",EDGE,"E26"),sQuery(id+"F4.wireOp",EDGE,"E27"),sQuery(id+"F4.wireOp",EDGE,"E28"),sQuery(id+"F4.wireOp",EDGE,"E30"),sQuery(id+"F4.wireOp",EDGE,"E31"),sQuery(id+"F4.wireOp",EDGE,"E32"),sQuery(id+"F4.wireOp",EDGE,"E33.trimOffspring")])]}),"instanceName":"1"});
            var Q2;
            Q2=makeQuery(id+"F1.opExtrude","SWEPT_BODY",BODY,{"disambiguationData":[OSD([sQuery(id+"F0.wireOp",EDGE,"E0.top"),sQuery(id+"F0.wireOp",EDGE,"E1"),sQuery(id+"F0.wireOp",EDGE,"E2"),sQuery(id+"F0.wireOp",EDGE,"E4"),sQuery(id+"F0.wireOp",EDGE,"E5"),sQuery(id+"F0.wireOp",EDGE,"E6"),sQuery(id+"F0.wireOp",EDGE,"E7"),sQuery(id+"F0.wireOp",EDGE,"E8"),sQuery(id+"F0.wireOp",EDGE,"E9"),sQuery(id+"F0.wireOp",EDGE,"E10"),sQuery(id+"F0.wireOp",EDGE,"E11"),sQuery(id+"F0.wireOp",EDGE,"E12.trimOffspring"),sQuery(id+"F0.wireOp",EDGE,"E13"),sQuery(id+"F0.wireOp",EDGE,"E14.trimOffspring"),sQuery(id+"F0.wireOp",EDGE,"E15"),sQuery(id+"F0.wireOp",EDGE,"E16"),sQuery(id+"F0.wireOp",EDGE,"E17")])]});
            deleteBodies(context, id + "F35", {"entities" : qUnion([Q0, Q1, Q2])});
        }
        {
            var Q0;
            Q0=qCreatedBy(makeId("Right.planeOp"),FACE);
            var sketch = newSketch(context, id + "F36", { "sketchPlane" : qUnion([Q0])});
            skLineSegment(sketch, "E88", {"start": v(0, 0) * mm, "end": v(-78.77, 0) * mm});
            skSolve(sketch);
        }
        {
            var Q0;
            Q0=makeQuery(id+"F29.opExtrude","SWEPT_BODY",BODY,{"disambiguationData":[OSD([sQuery(id+"F28.wireOp",EDGE,"E59"),sQuery(id+"F28.wireOp",EDGE,"E61"),sQuery(id+"F28.wireOp",EDGE,"E58"),sQuery(id+"F28.wireOp",EDGE,"E63"),sQuery(id+"F28.wireOp",EDGE,"E64"),sQuery(id+"F28.wireOp",EDGE,"E65"),sQuery(id+"F28.wireOp",EDGE,"E66"),sQuery(id+"F28.wireOp",EDGE,"E67"),sQuery(id+"F28.wireOp",EDGE,"E69"),sQuery(id+"F28.wireOp",EDGE,"E70"),sQuery(id+"F28.wireOp",EDGE,"E71"),sQuery(id+"F28.wireOp",EDGE,"E72"),sQuery(id+"F28.wireOp",EDGE,"E73"),sQuery(id+"F28.wireOp",EDGE,"E74"),sQuery(id+"F28.wireOp",EDGE,"E75"),sQuery(id+"F28.wireOp",EDGE,"E76"),sQuery(id+"F28.wireOp",EDGE,"E77"),sQuery(id+"F28.wireOp",EDGE,"E80"),sQuery(id+"F28.wireOp",EDGE,"E81"),sQuery(id+"F28.wireOp",EDGE,"E82")])]});
            var Q1;
            Q1=sQuery(id+"F36.wireOp",EDGE,"E88");
            transform(context, id + "F37", {"entities" : qUnion([Q0]), "transformType" : TransformType.ROTATION, "transformAxis" : qUnion([Q1]), "angle" : 90 * degree, "makeCopy" : false});
        }
        {
            var Q0;
            Q0=makeQuery(id+"F29.opExtrude","SWEPT_BODY",BODY,{"disambiguationData":[OSD([sQuery(id+"F28.wireOp",EDGE,"E59"),sQuery(id+"F28.wireOp",EDGE,"E61"),sQuery(id+"F28.wireOp",EDGE,"E58"),sQuery(id+"F28.wireOp",EDGE,"E63"),sQuery(id+"F28.wireOp",EDGE,"E64"),sQuery(id+"F28.wireOp",EDGE,"E65"),sQuery(id+"F28.wireOp",EDGE,"E66"),sQuery(id+"F28.wireOp",EDGE,"E67"),sQuery(id+"F28.wireOp",EDGE,"E69"),sQuery(id+"F28.wireOp",EDGE,"E70"),sQuery(id+"F28.wireOp",EDGE,"E71"),sQuery(id+"F28.wireOp",EDGE,"E72"),sQuery(id+"F28.wireOp",EDGE,"E73"),sQuery(id+"F28.wireOp",EDGE,"E74"),sQuery(id+"F28.wireOp",EDGE,"E75"),sQuery(id+"F28.wireOp",EDGE,"E76"),sQuery(id+"F28.wireOp",EDGE,"E77"),sQuery(id+"F28.wireOp",EDGE,"E80"),sQuery(id+"F28.wireOp",EDGE,"E81"),sQuery(id+"F28.wireOp",EDGE,"E82")])]});
            transform(context, id + "F38", {"entities" : qUnion([Q0]), "transformType" : TransformType.TRANSLATION_3D, "dx" : 120 * mm, "dy" : -60 * mm, "dz" : 0 * mm, "makeCopy" : false});
        }
        {
            var Q0;
            Q0=makeQuery(id+"F29.opExtrude","SWEPT_BODY",BODY,{"disambiguationData":[OSD([sQuery(id+"F28.wireOp",EDGE,"E59"),sQuery(id+"F28.wireOp",EDGE,"E61"),sQuery(id+"F28.wireOp",EDGE,"E58"),sQuery(id+"F28.wireOp",EDGE,"E63"),sQuery(id+"F28.wireOp",EDGE,"E64"),sQuery(id+"F28.wireOp",EDGE,"E65"),sQuery(id+"F28.wireOp",EDGE,"E66"),sQuery(id+"F28.wireOp",EDGE,"E67"),sQuery(id+"F28.wireOp",EDGE,"E69"),sQuery(id+"F28.wireOp",EDGE,"E70"),sQuery(id+"F28.wireOp",EDGE,"E71"),sQuery(id+"F28.wireOp",EDGE,"E72"),sQuery(id+"F28.wireOp",EDGE,"E73"),sQuery(id+"F28.wireOp",EDGE,"E74"),sQuery(id+"F28.wireOp",EDGE,"E75"),sQuery(id+"F28.wireOp",EDGE,"E76"),sQuery(id+"F28.wireOp",EDGE,"E77"),sQuery(id+"F28.wireOp",EDGE,"E80"),sQuery(id+"F28.wireOp",EDGE,"E81"),sQuery(id+"F28.wireOp",EDGE,"E82")])]});
            var Q1;
            Q1=qCreatedBy(makeId("Right.planeOp"),FACE);
            mirror(context, id + "F39", {"entities" : qUnion([Q0]), "mirrorPlane" : qUnion([Q1])});
        }
        {
            var Q0;
            Q0=qCreatedBy(makeId("Top.planeOp"),FACE);
            var sketch = newSketch(context, id + "F40", { "sketchPlane" : qUnion([Q0])});
            skLineSegment(sketch, "E89", {"start": v(30, 25) * mm, "end": v(30, 15) * mm});
            skLineSegment(sketch, "E90", {"start": v(30, 15) * mm, "end": v(-30, 15) * mm});
            skLineSegment(sketch, "E91", {"start": v(-30, 15) * mm, "end": v(-30, 25) * mm});
            skLineSegment(sketch, "E92", {"start": v(-30, 25) * mm, "end": v(30, 25) * mm});
            skCircle(sketch, "E93", {"center": v(-25, 20) * mm, "radius": 2 * mm});
            skCircle(sketch, "E94", {"center": v(-10, 20) * mm, "radius": 2 * mm});
            skCircle(sketch, "E95", {"center": v(10, 20) * mm, "radius": 2 * mm});
            skCircle(sketch, "E96", {"center": v(25, 20) * mm, "radius": 2 * mm});
            skPoint(sketch, "E97.end.orphan", {"position": v(-30, 20) * mm});
            skSolve(sketch);
        }
        {
            var Q0;
            Q0=qSketchRegion(id+"F40",true);
            extrude(context, id + "F41", {"entities" : qUnion([Q0]), "depth" : 8 * mm});
        }
        {
            var Q0;
            Q0=makeQuery(id+"F41.opExtrude","SWEPT_BODY",BODY,{"disambiguationData":[OSD([sQuery(id+"F40.wireOp",EDGE,"E89"),sQuery(id+"F40.wireOp",EDGE,"E90"),sQuery(id+"F40.wireOp",EDGE,"E91"),sQuery(id+"F40.wireOp",EDGE,"E92"),sQuery(id+"F40.wireOp",EDGE,"E93"),sQuery(id+"F40.wireOp",EDGE,"E94"),sQuery(id+"F40.wireOp",EDGE,"E95"),sQuery(id+"F40.wireOp",EDGE,"E96")])]});
            transform(context, id + "F42", {"entities" : qUnion([Q0]), "transformType" : TransformType.TRANSLATION_3D, "dx" : 0 * mm, "dy" : 0 * mm, "dz" : 8 * mm, "makeCopy" : false});
        }
        {
            var Q0;
            Q0=makeQuery(id+"F41.opExtrude","CAP_EDGE",EDGE,{"disambiguationData":[OSD([sQuery(id+"F40.wireOp",EDGE,"E90")])],"isStart":false});
            var Q1;
            Q1=makeQuery(id+"F41.opExtrude","SWEPT_EDGE",EDGE,{"disambiguationData":[OSD([sQuery(id+"F40.wireOp",EDGE,"E89"),sQuery(id+"F40.wireOp",EDGE,"E90")])]});
            var Q2;
            Q2=makeQuery(id+"F41.opExtrude","SWEPT_EDGE",EDGE,{"disambiguationData":[OSD([sQuery(id+"F40.wireOp",EDGE,"E89"),sQuery(id+"F40.wireOp",EDGE,"E92")])]});
            var Q3;
            Q3=makeQuery(id+"F41.opExtrude","CAP_EDGE",EDGE,{"disambiguationData":[OSD([sQuery(id+"F40.wireOp",EDGE,"E89")])],"isStart":false});
            var Q4;
            Q4=makeQuery(id+"F41.opExtrude","CAP_EDGE",EDGE,{"disambiguationData":[OSD([sQuery(id+"F40.wireOp",EDGE,"E91")])],"isStart":false});
            var Q5;
            Q5=makeQuery(id+"F41.opExtrude","SWEPT_EDGE",EDGE,{"disambiguationData":[OSD([sQuery(id+"F40.wireOp",EDGE,"E90"),sQuery(id+"F40.wireOp",EDGE,"E91")])]});
            var Q6;
            Q6=makeQuery(id+"F41.opExtrude","SWEPT_EDGE",EDGE,{"disambiguationData":[OSD([sQuery(id+"F40.wireOp",EDGE,"E91"),sQuery(id+"F40.wireOp",EDGE,"E92")])]});
            var Q7;
            Q7=makeQuery(id+"F41.opExtrude","CAP_EDGE",EDGE,{"disambiguationData":[OSD([sQuery(id+"F40.wireOp",EDGE,"E92")])],"isStart":false});
            fillet(context, id + "F43", {"entities" : qUnion([Q0, Q1, Q2, Q3, Q4, Q5, Q6, Q7]), "radius" : 1.5 * mm, "tangentPropagation" : true, "allowEdgeOverflow" : false});
        }
        {
            var Q0;
            Q0=makeQuery(id+"F39.opPattern","COPY",BODY,{"derivedFrom":makeQuery(id+"F29.opExtrude","SWEPT_BODY",BODY,{"disambiguationData":[OSD([sQuery(id+"F28.wireOp",EDGE,"E59"),sQuery(id+"F28.wireOp",EDGE,"E61"),sQuery(id+"F28.wireOp",EDGE,"E58"),sQuery(id+"F28.wireOp",EDGE,"E63"),sQuery(id+"F28.wireOp",EDGE,"E64"),sQuery(id+"F28.wireOp",EDGE,"E65"),sQuery(id+"F28.wireOp",EDGE,"E66"),sQuery(id+"F28.wireOp",EDGE,"E67"),sQuery(id+"F28.wireOp",EDGE,"E69"),sQuery(id+"F28.wireOp",EDGE,"E70"),sQuery(id+"F28.wireOp",EDGE,"E71"),sQuery(id+"F28.wireOp",EDGE,"E72"),sQuery(id+"F28.wireOp",EDGE,"E73"),sQuery(id+"F28.wireOp",EDGE,"E74"),sQuery(id+"F28.wireOp",EDGE,"E75"),sQuery(id+"F28.wireOp",EDGE,"E76"),sQuery(id+"F28.wireOp",EDGE,"E77"),sQuery(id+"F28.wireOp",EDGE,"E80"),sQuery(id+"F28.wireOp",EDGE,"E81"),sQuery(id+"F28.wireOp",EDGE,"E82")])]}),"instanceName":"1"});
            var Q1;
            Q1=makeQuery(id+"F41.opExtrude","SWEPT_BODY",BODY,{"disambiguationData":[OSD([sQuery(id+"F40.wireOp",EDGE,"E89"),sQuery(id+"F40.wireOp",EDGE,"E90"),sQuery(id+"F40.wireOp",EDGE,"E91"),sQuery(id+"F40.wireOp",EDGE,"E92"),sQuery(id+"F40.wireOp",EDGE,"E93"),sQuery(id+"F40.wireOp",EDGE,"E94"),sQuery(id+"F40.wireOp",EDGE,"E95"),sQuery(id+"F40.wireOp",EDGE,"E96")])]});
            deleteBodies(context, id + "F44", {"entities" : qUnion([Q0, Q1])});
        }
        {
            var Q0;
            Q0=makeQuery(id+"F29.opExtrude","SWEPT_BODY",BODY,{"disambiguationData":[OSD([sQuery(id+"F28.wireOp",EDGE,"E59"),sQuery(id+"F28.wireOp",EDGE,"E61"),sQuery(id+"F28.wireOp",EDGE,"E58"),sQuery(id+"F28.wireOp",EDGE,"E63"),sQuery(id+"F28.wireOp",EDGE,"E64"),sQuery(id+"F28.wireOp",EDGE,"E65"),sQuery(id+"F28.wireOp",EDGE,"E66"),sQuery(id+"F28.wireOp",EDGE,"E67"),sQuery(id+"F28.wireOp",EDGE,"E69"),sQuery(id+"F28.wireOp",EDGE,"E70"),sQuery(id+"F28.wireOp",EDGE,"E71"),sQuery(id+"F28.wireOp",EDGE,"E72"),sQuery(id+"F28.wireOp",EDGE,"E73"),sQuery(id+"F28.wireOp",EDGE,"E74"),sQuery(id+"F28.wireOp",EDGE,"E75"),sQuery(id+"F28.wireOp",EDGE,"E76"),sQuery(id+"F28.wireOp",EDGE,"E77"),sQuery(id+"F28.wireOp",EDGE,"E80"),sQuery(id+"F28.wireOp",EDGE,"E81"),sQuery(id+"F28.wireOp",EDGE,"E82")])]});
            transform(context, id + "F45", {"entities" : qUnion([Q0]), "transformType" : TransformType.TRANSLATION_3D, "dx" : -50 * mm, "dy" : 0 * mm, "dz" : 0 * mm, "makeCopy" : false});
        }
    });
